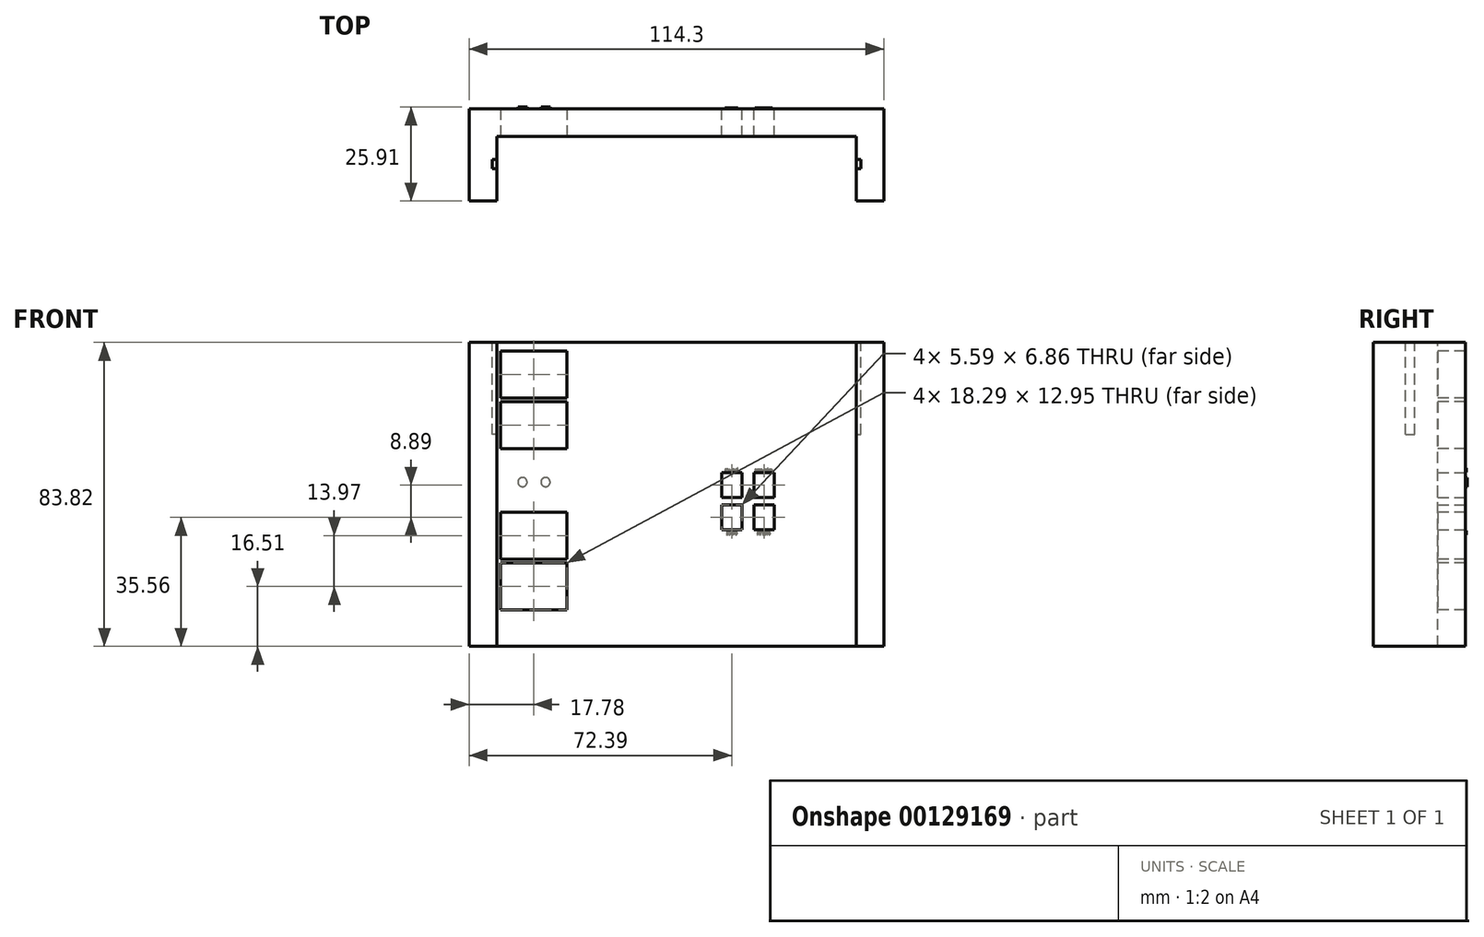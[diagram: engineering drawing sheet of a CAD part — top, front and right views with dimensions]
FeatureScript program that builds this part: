
annotation { "Feature Type Name" : "Feature", "Feature Type Description" : "" }
export const myFeature = defineFeature(function(context is Context, id is Id, definition is map)
    precondition{}
    {
        {
            var Q0;
            Q0=qCreatedBy(makeId("Front.planeOp"),FACE);
            var sketch = newSketch(context, id + "F0", { "sketchPlane" : qUnion([Q0])});
            skLineSegment(sketch, "E0.bottom", {"start": v(57.15, 41.91) * mm, "end": v(-57.15, 41.91) * mm});
            skLineSegment(sketch, "E0.top", {"start": v(57.15, -41.91) * mm, "end": v(-57.15, -41.91) * mm});
            skLineSegment(sketch, "E0.left", {"start": v(57.15, 41.91) * mm, "end": v(57.15, -41.91) * mm});
            skLineSegment(sketch, "E0.right", {"start": v(-57.15, 41.91) * mm, "end": v(-57.15, -41.91) * mm});
            skPoint(sketch, "E0.middle", {"position": v(0, 0) * mm});
            skSolve(sketch);
        }
        {
            var Q0;
            Q0=makeQuery(id+"F0.imprint","IMPRINT",FACE,{"disambiguationData":[TD([[makeQuery(id+"F0.imprint","IMPRINT",EDGE,{"derivedFrom":sQuery(id+"F0.wireOp",EDGE,"E0.bottom")}),1.0]])]});
            extrude(context, id + "F1", {"entities" : qUnion([Q0]), "depth" : 7.62 * mm});
        }
        {
            var Q0;
            Q0=makeQuery(id+"F1.opExtrude","CAP_FACE",FACE,{"disambiguationData":[OSD([sQuery(id+"F0.wireOp",EDGE,"E0.bottom"),sQuery(id+"F0.wireOp",EDGE,"E0.top"),sQuery(id+"F0.wireOp",EDGE,"E0.left"),sQuery(id+"F0.wireOp",EDGE,"E0.right")])],"isStart":false});
            var sketch = newSketch(context, id + "F2", { "sketchPlane" : qUnion([Q0])});
            skLineSegment(sketch, "E1.bottom", {"start": v(-57.15, 41.91) * mm, "end": v(-49.53, 41.91) * mm});
            skLineSegment(sketch, "E1.top", {"start": v(-57.15, -41.91) * mm, "end": v(-49.53, -41.91) * mm});
            skLineSegment(sketch, "E1.left", {"start": v(-57.15, 41.91) * mm, "end": v(-57.15, -41.91) * mm});
            skLineSegment(sketch, "E1.right", {"start": v(-49.53, 41.91) * mm, "end": v(-49.53, -41.91) * mm});
            skLineSegment(sketch, "E2.bottom", {"start": v(57.15, -41.91) * mm, "end": v(49.53, -41.91) * mm});
            skLineSegment(sketch, "E2.top", {"start": v(57.15, 41.91) * mm, "end": v(49.53, 41.91) * mm});
            skLineSegment(sketch, "E2.left", {"start": v(57.15, -41.91) * mm, "end": v(57.15, 41.91) * mm});
            skLineSegment(sketch, "E2.right", {"start": v(49.53, -41.91) * mm, "end": v(49.53, 41.91) * mm});
            skSolve(sketch);
        }
        {
            var Q0;
            Q0=makeQuery(id+"F2.imprint","IMPRINT",FACE,{"disambiguationData":[TD([[makeQuery(id+"F2.imprint","IMPRINT",EDGE,{"derivedFrom":sQuery(id+"F2.wireOp",EDGE,"E1.bottom")}),1.0]])]});
            var Q1;
            Q1=makeQuery(id+"F2.imprint","IMPRINT",FACE,{"disambiguationData":[TD([[makeQuery(id+"F2.imprint","IMPRINT",EDGE,{"derivedFrom":sQuery(id+"F2.wireOp",EDGE,"E2.bottom")}),-1.0]])]});
            extrude(context, id + "F3", {"entities" : qUnion([Q0, Q1]), "operationType" : NewBodyOperationType.ADD, "depth" : 17.78 * mm});
        }
        {
            var Q0;
            Q0=makeQuery(id+"F3.boolean.opBoolean","MERGE",FACE,{"derivedFrom":[makeQuery(id+"F1.opExtrude","SWEPT_FACE",FACE,{"disambiguationData":[OSD([sQuery(id+"F0.wireOp",EDGE,"E0.bottom")])]}),makeQuery(id+"F3.opExtrude","SWEPT_FACE",FACE,{"disambiguationData":[OSD([sQuery(id+"F2.wireOp",EDGE,"E1.bottom")])]}),makeQuery(id+"F3.opExtrude","SWEPT_FACE",FACE,{"disambiguationData":[OSD([sQuery(id+"F2.wireOp",EDGE,"E2.top")])]})]});
            var sketch = newSketch(context, id + "F4", { "sketchPlane" : qUnion([Q0])});
            skLineSegment(sketch, "E3.bottom", {"start": v(-49.53, -16.51) * mm, "end": v(-50.8, -16.51) * mm});
            skLineSegment(sketch, "E3.top", {"start": v(-49.53, -13.97) * mm, "end": v(-50.8, -13.97) * mm});
            skLineSegment(sketch, "E3.left", {"start": v(-49.53, -16.51) * mm, "end": v(-49.53, -13.97) * mm});
            skLineSegment(sketch, "E3.right", {"start": v(-50.8, -16.51) * mm, "end": v(-50.8, -13.97) * mm});
            skLineSegment(sketch, "E4.bottom", {"start": v(49.53, -13.97) * mm, "end": v(50.8, -13.97) * mm});
            skLineSegment(sketch, "E4.top", {"start": v(49.53, -16.5) * mm, "end": v(50.8, -16.5) * mm});
            skLineSegment(sketch, "E4.left", {"start": v(49.53, -13.97) * mm, "end": v(49.53, -16.5) * mm});
            skLineSegment(sketch, "E4.right", {"start": v(50.8, -13.97) * mm, "end": v(50.8, -16.5) * mm});
            skSolve(sketch);
        }
        {
            var Q0;
            Q0=makeQuery(id+"F4.imprint","IMPRINT",FACE,{"disambiguationData":[TD([[makeQuery(id+"F4.imprint","IMPRINT",EDGE,{"derivedFrom":sQuery(id+"F4.wireOp",EDGE,"E3.bottom")}),-1.0]])]});
            var Q1;
            Q1=makeQuery(id+"F4.imprint","IMPRINT",FACE,{"disambiguationData":[TD([[makeQuery(id+"F4.imprint","IMPRINT",EDGE,{"derivedFrom":sQuery(id+"F4.wireOp",EDGE,"E4.bottom")}),-1.0]])]});
            extrude(context, id + "F5", {"entities" : qUnion([Q0, Q1]), "operationType" : NewBodyOperationType.REMOVE, "oppositeDirection" : true, "depth" : 25.4 * mm});
        }
        {
            var Q0;
            Q0=makeQuery(id+"F1.opExtrude","CAP_FACE",FACE,{"disambiguationData":[OSD([sQuery(id+"F0.wireOp",EDGE,"E0.bottom"),sQuery(id+"F0.wireOp",EDGE,"E0.top"),sQuery(id+"F0.wireOp",EDGE,"E0.left"),sQuery(id+"F0.wireOp",EDGE,"E0.right")])],"isStart":false});
            var sketch = newSketch(context, id + "F6", { "sketchPlane" : qUnion([Q0])});
            skPoint(sketch, "E5", {"position": v(-39.37, 41.91) * mm});
            skPoint(sketch, "E6", {"position": v(-39.37, 33.02) * mm});
            skLineSegment(sketch, "E7.bottom", {"start": v(-30.23, 39.5) * mm, "end": v(-48.51, 39.5) * mm});
            skLineSegment(sketch, "E7.top", {"start": v(-30.23, 26.54) * mm, "end": v(-48.51, 26.54) * mm});
            skLineSegment(sketch, "E7.left", {"start": v(-30.23, 39.5) * mm, "end": v(-30.23, 26.54) * mm});
            skLineSegment(sketch, "E7.right", {"start": v(-48.51, 39.5) * mm, "end": v(-48.51, 26.54) * mm});
            skPoint(sketch, "E8", {"position": v(-39.37, 19.05) * mm});
            skLineSegment(sketch, "E9.bottom", {"start": v(-30.23, 25.53) * mm, "end": v(-48.51, 25.53) * mm});
            skLineSegment(sketch, "E9.top", {"start": v(-30.23, 12.57) * mm, "end": v(-48.51, 12.57) * mm});
            skLineSegment(sketch, "E9.left", {"start": v(-30.23, 25.53) * mm, "end": v(-30.23, 12.57) * mm});
            skLineSegment(sketch, "E9.right", {"start": v(-48.51, 25.53) * mm, "end": v(-48.51, 12.57) * mm});
            skPoint(sketch, "E10", {"position": v(-39.37, -41.91) * mm});
            skPoint(sketch, "E11", {"position": v(-39.37, -11.43) * mm});
            skLineSegment(sketch, "E12.bottom", {"start": v(-30.23, -4.95) * mm, "end": v(-48.51, -4.95) * mm});
            skLineSegment(sketch, "E12.top", {"start": v(-30.23, -17.9) * mm, "end": v(-48.51, -17.9) * mm});
            skLineSegment(sketch, "E12.left", {"start": v(-30.23, -4.95) * mm, "end": v(-30.23, -17.9) * mm});
            skLineSegment(sketch, "E12.right", {"start": v(-48.51, -4.95) * mm, "end": v(-48.51, -17.9) * mm});
            skPoint(sketch, "E13", {"position": v(-39.37, -25.4) * mm});
            skLineSegment(sketch, "E14.bottom", {"start": v(-30.23, -18.92) * mm, "end": v(-48.51, -18.92) * mm});
            skLineSegment(sketch, "E14.top", {"start": v(-30.23, -31.88) * mm, "end": v(-48.51, -31.88) * mm});
            skLineSegment(sketch, "E14.left", {"start": v(-30.23, -18.92) * mm, "end": v(-30.23, -31.88) * mm});
            skLineSegment(sketch, "E14.right", {"start": v(-48.51, -18.92) * mm, "end": v(-48.51, -31.88) * mm});
            skPoint(sketch, "E15", {"position": v(-39.37, 39.5) * mm});
            skSolve(sketch);
        }
        {
            var Q0;
            Q0 = qSketchRegion(id + "F6", true);
            extrude(context, id + "F7", {"entities" : qUnion([Q0]), "operationType" : NewBodyOperationType.REMOVE, "oppositeDirection" : true, "depth" : 25.4 * mm});
        }
        {
            var Q0;
            Q0=makeQuery(id+"F1.opExtrude","CAP_FACE",FACE,{"disambiguationData":[OSD([sQuery(id+"F0.wireOp",EDGE,"E0.bottom"),sQuery(id+"F0.wireOp",EDGE,"E0.top"),sQuery(id+"F0.wireOp",EDGE,"E0.left"),sQuery(id+"F0.wireOp",EDGE,"E0.right")])],"isStart":true});
            var sketch = newSketch(context, id + "F8", { "sketchPlane" : qUnion([Q0])});
            skPoint(sketch, "E16", {"position": v(-15.24, -6.35) * mm});
            skPoint(sketch, "E17", {"position": v(-15.24, 2.54) * mm});
            skPoint(sketch, "E18", {"position": v(-15.24, -41.91) * mm});
            skPoint(sketch, "E19", {"position": v(57.15, 2.54) * mm});
            skPoint(sketch, "E20", {"position": v(-24.13, 2.54) * mm});
            skPoint(sketch, "E21", {"position": v(-24.13, -6.35) * mm});
            skPoint(sketch, "E22", {"position": v(57.15, -6.35) * mm});
            skLineSegment(sketch, "E23.bottom", {"start": v(-26.92, 5.97) * mm, "end": v(-21.34, 5.97) * mm});
            skLineSegment(sketch, "E23.top", {"start": v(-26.92, -0.89) * mm, "end": v(-21.34, -0.89) * mm});
            skLineSegment(sketch, "E23.left", {"start": v(-26.92, 5.97) * mm, "end": v(-26.92, -0.89) * mm});
            skLineSegment(sketch, "E23.right", {"start": v(-21.34, 5.97) * mm, "end": v(-21.34, -0.89) * mm});
            skLineSegment(sketch, "E24.bottom", {"start": v(-26.92, -2.92) * mm, "end": v(-21.34, -2.92) * mm});
            skLineSegment(sketch, "E24.top", {"start": v(-26.92, -9.78) * mm, "end": v(-21.34, -9.78) * mm});
            skLineSegment(sketch, "E24.left", {"start": v(-26.92, -2.92) * mm, "end": v(-26.92, -9.78) * mm});
            skLineSegment(sketch, "E24.right", {"start": v(-21.34, -2.92) * mm, "end": v(-21.34, -9.78) * mm});
            skLineSegment(sketch, "E25.bottom", {"start": v(-18.03, 5.97) * mm, "end": v(-12.45, 5.97) * mm});
            skLineSegment(sketch, "E25.top", {"start": v(-18.03, -0.89) * mm, "end": v(-12.45, -0.89) * mm});
            skLineSegment(sketch, "E25.left", {"start": v(-18.03, 5.97) * mm, "end": v(-18.03, -0.89) * mm});
            skLineSegment(sketch, "E25.right", {"start": v(-12.45, 5.97) * mm, "end": v(-12.45, -0.89) * mm});
            skLineSegment(sketch, "E26.bottom", {"start": v(-18.03, -2.92) * mm, "end": v(-12.45, -2.92) * mm});
            skLineSegment(sketch, "E26.top", {"start": v(-18.03, -9.78) * mm, "end": v(-12.45, -9.78) * mm});
            skLineSegment(sketch, "E26.left", {"start": v(-18.03, -2.92) * mm, "end": v(-18.03, -9.78) * mm});
            skLineSegment(sketch, "E26.right", {"start": v(-12.45, -2.92) * mm, "end": v(-12.45, -9.78) * mm});
            skSolve(sketch);
        }
        {
            var Q0;
            Q0=makeQuery(id+"F8.imprint","IMPRINT",FACE,{"disambiguationData":[TD([[makeQuery(id+"F8.imprint","IMPRINT",EDGE,{"derivedFrom":sQuery(id+"F8.wireOp",EDGE,"E23.bottom")}),-1.0]])]});
            var Q1;
            Q1=makeQuery(id+"F8.imprint","IMPRINT",FACE,{"disambiguationData":[TD([[makeQuery(id+"F8.imprint","IMPRINT",EDGE,{"derivedFrom":sQuery(id+"F8.wireOp",EDGE,"E25.bottom")}),-1.0]])]});
            var Q2;
            Q2=makeQuery(id+"F8.imprint","IMPRINT",FACE,{"disambiguationData":[TD([[makeQuery(id+"F8.imprint","IMPRINT",EDGE,{"derivedFrom":sQuery(id+"F8.wireOp",EDGE,"E24.bottom")}),-1.0]])]});
            var Q3;
            Q3=makeQuery(id+"F8.imprint","IMPRINT",FACE,{"disambiguationData":[TD([[makeQuery(id+"F8.imprint","IMPRINT",EDGE,{"derivedFrom":sQuery(id+"F8.wireOp",EDGE,"E26.bottom")}),-1.0]])]});
            extrude(context, id + "F9", {"entities" : qUnion([Q0, Q1, Q2, Q3]), "operationType" : NewBodyOperationType.REMOVE, "oppositeDirection" : true, "depth" : 25.4 * mm});
        }
        {
            var Q0;
            Q0=makeQuery(id+"F1.opExtrude","CAP_FACE",FACE,{"disambiguationData":[OSD([sQuery(id+"F0.wireOp",EDGE,"E0.bottom"),sQuery(id+"F0.wireOp",EDGE,"E0.top"),sQuery(id+"F0.wireOp",EDGE,"E0.left"),sQuery(id+"F0.wireOp",EDGE,"E0.right")])],"isStart":true});
            var sketch = newSketch(context, id + "F10", { "sketchPlane" : qUnion([Q0])});
            skText(sketch, "E27", { "text": "hours", "fontName": "OpenSans-Regular.ttf"});
            const initialGuessF10  = {"E27": [-0.01704, 0.00622, 1, 0, 0.001]};
            skSetInitialGuess(sketch, initialGuessF10);
            skSolve(sketch);
        }
        {
            var Q0;
            Q0 = qSketchRegion(id + "F10", true);
            extrude(context, id + "F11", {"entities" : qUnion([Q0]), "operationType" : NewBodyOperationType.ADD, "depth" : 0.25 * mm});
        }
        {
            var Q0;
            {var subQ0=sQuery(id+"F0.wireOp",EDGE,"E0.top");var subQ1=sQuery(id+"F0.wireOp",EDGE,"E0.left");var subQ2=sQuery(id+"F0.wireOp",EDGE,"E0.bottom");var subQ3=sQuery(id+"F0.wireOp",EDGE,"E0.right");Q0=makeQuery(id+"F11.boolean.opBoolean","SPLIT",FACE,{"disambiguationData":[TD([makeQuery(id+"F1.opExtrude","SWEPT_FACE",FACE,{"disambiguationData":[OSD([subQ2])]})])],"derivedFrom":makeQuery(id+"F1.opExtrude","CAP_FACE",FACE,{"disambiguationData":[OSD([subQ2,subQ0,subQ1,subQ3])],"isStart":true})});}
            var sketch = newSketch(context, id + "F12", { "sketchPlane" : qUnion([Q0])});
            skText(sketch, "E28", { "text": "minutes", "fontName": "OpenSans-Regular.ttf"});
            const initialGuessF12  = {"E28": [-0.0266, 0.00619, 1, 0, 0.00096]};
            skSetInitialGuess(sketch, initialGuessF12);
            skSolve(sketch);
        }
        {
            var Q0;
            Q0 = qSketchRegion(id + "F12", true);
            extrude(context, id + "F13", {"entities" : qUnion([Q0]), "operationType" : NewBodyOperationType.ADD, "depth" : 0.25 * mm});
        }
        {
            var Q0;
            {var subQ57=sQuery(id+"F0.wireOp",EDGE,"E0.right");var subQ78=sQuery(id+"F0.wireOp",EDGE,"E0.bottom");var subQ79=makeQuery(id+"F1.opExtrude","SWEPT_FACE",FACE,{"disambiguationData":[OSD([subQ78])]});var subQ99=sQuery(id+"F0.wireOp",EDGE,"E0.left");var subQ101=sQuery(id+"F0.wireOp",EDGE,"E0.top");Q0=makeQuery(id+"F13.boolean.opBoolean","SPLIT",FACE,{"disambiguationData":[TD([subQ79])],"derivedFrom":makeQuery(id+"F11.boolean.opBoolean","SPLIT",FACE,{"disambiguationData":[TD([subQ79])],"derivedFrom":makeQuery(id+"F1.opExtrude","CAP_FACE",FACE,{"disambiguationData":[OSD([subQ78,subQ101,subQ99,subQ57])],"isStart":true})})});}
            var sketch = newSketch(context, id + "F14", { "sketchPlane" : qUnion([Q0])});
            skText(sketch, "E29", { "text": "alarm", "fontName": "OpenSans-Regular.ttf"});
            skPoint(sketch, "E30", {"position": v(-24.13, -9.78) * mm});
            const initialGuessF14  = {"E29": [-0.02596, -0.01107, 1, 0, 0.00102]};
            skSetInitialGuess(sketch, initialGuessF14);
            skSolve(sketch);
        }
        {
            var Q0;
            Q0 = qSketchRegion(id + "F14", true);
            extrude(context, id + "F15", {"entities" : qUnion([Q0]), "operationType" : NewBodyOperationType.ADD, "depth" : 0.25 * mm});
        }
        {
            var Q0;
            {var subQ136=sQuery(id+"F0.wireOp",EDGE,"E0.right");var subQ161=sQuery(id+"F0.wireOp",EDGE,"E0.bottom");var subQ162=makeQuery(id+"F1.opExtrude","SWEPT_FACE",FACE,{"disambiguationData":[OSD([subQ161])]});var subQ189=sQuery(id+"F0.wireOp",EDGE,"E0.left");var subQ193=sQuery(id+"F0.wireOp",EDGE,"E0.top");Q0=makeQuery(id+"F15.boolean.opBoolean","SPLIT",FACE,{"disambiguationData":[TD([subQ162])],"derivedFrom":makeQuery(id+"F13.boolean.opBoolean","SPLIT",FACE,{"disambiguationData":[TD([subQ162])],"derivedFrom":makeQuery(id+"F11.boolean.opBoolean","SPLIT",FACE,{"disambiguationData":[TD([subQ162])],"derivedFrom":makeQuery(id+"F1.opExtrude","CAP_FACE",FACE,{"disambiguationData":[OSD([subQ161,subQ193,subQ189,subQ136])],"isStart":true})})})});}
            var sketch = newSketch(context, id + "F16", { "sketchPlane" : qUnion([Q0])});
            skText(sketch, "E31", { "text": "clock", "fontName": "OpenSans-Regular.ttf"});
            skPoint(sketch, "E32", {"position": v(-15.24, -9.78) * mm});
            const initialGuessF16  = {"E31": [-0.01685, -0.01108, 1, 0, 0.00097]};
            skSetInitialGuess(sketch, initialGuessF16);
            skSolve(sketch);
        }
        {
            var Q0;
            Q0 = qSketchRegion(id + "F16", true);
            extrude(context, id + "F17", {"entities" : qUnion([Q0]), "operationType" : NewBodyOperationType.ADD, "depth" : 0.25 * mm});
        }
        {
            var Q0;
            {var subQ153=sQuery(id+"F0.wireOp",EDGE,"E0.right");var subQ179=sQuery(id+"F0.wireOp",EDGE,"E0.bottom");var subQ180=makeQuery(id+"F1.opExtrude","SWEPT_FACE",FACE,{"disambiguationData":[OSD([subQ179])]});var subQ211=sQuery(id+"F0.wireOp",EDGE,"E0.left");var subQ215=sQuery(id+"F0.wireOp",EDGE,"E0.top");Q0=makeQuery(id+"F17.boolean.opBoolean","SPLIT",FACE,{"disambiguationData":[TD([subQ180])],"derivedFrom":makeQuery(id+"F15.boolean.opBoolean","SPLIT",FACE,{"disambiguationData":[TD([subQ180])],"derivedFrom":makeQuery(id+"F13.boolean.opBoolean","SPLIT",FACE,{"disambiguationData":[TD([subQ180])],"derivedFrom":makeQuery(id+"F11.boolean.opBoolean","SPLIT",FACE,{"disambiguationData":[TD([subQ180])],"derivedFrom":makeQuery(id+"F1.opExtrude","CAP_FACE",FACE,{"disambiguationData":[OSD([subQ179,subQ215,subQ211,subQ153])],"isStart":true})})})})});}
            var sketch = newSketch(context, id + "F18", { "sketchPlane" : qUnion([Q0])});
            skCircle(sketch, "E33", {"center": v(42.42, 3.4) * mm, "radius": 1.27 * mm});
            skPoint(sketch, "E34.centerSnap0", {"position": v(39.37, -31.88) * mm});
            skPoint(sketch, "E35", {"position": v(42.42, -41.91) * mm});
            skCircle(sketch, "E36", {"center": v(36.07, 3.4) * mm, "radius": 1.27 * mm});
            skSolve(sketch);
        }
        {
            var Q0;
            Q0=makeQuery(id+"F18.imprint","IMPRINT",FACE,{"disambiguationData":[TD([[makeQuery(id+"F18.imprint","IMPRINT",EDGE,{"derivedFrom":sQuery(id+"F18.wireOp",EDGE,"E33")}),1.0]])]});
            var Q1;
            Q1=makeQuery(id+"F18.imprint","IMPRINT",FACE,{"disambiguationData":[TD([[makeQuery(id+"F18.imprint","IMPRINT",EDGE,{"derivedFrom":sQuery(id+"F18.wireOp",EDGE,"E36")}),1.0]])]});
            extrude(context, id + "F19", {"entities" : qUnion([Q0, Q1]), "operationType" : NewBodyOperationType.ADD, "depth" : 0.5 * mm});
        }
    });
